# Revit family: S-tank_FRESH-200
name_source: partatom
category: Оборудование
units: mm (PartAtom-declared; Revit-internal decimal feet)

## family parameters
Всегда вертикально = Да
Классификация = Нет
На основе рабочей плоскости = Нет
Общий = Нет
При загрузке вырезать с полостями = Нет
Размер круглого соединителя = Использовать диаметр
Тип детали = Нормальный
Точка расчета площади = Нет

## types (1)
- FRESH 200
    A = 210 мм
    ADSK_URL документации изделия = http://s-tank.ru
    ADSK_Группирование = Оборудование
    ADSK_Единица измерения = шт.
    ADSK_Завод-изготовитель = ООО “С-ТЭНК ВОТЕР ХИТЕРС”
    ADSK_Код изделия = 1.0200
    ADSK_Марка = FRESH 200
    ADSK_Масса = 51
    ADSK_Наименование = Буферная емкость c ГВС
    ADSK_Обозначение = FRESH 200
    B = 355 мм
    C = 465 мм
    D = 545 мм
    DN1 = 25 мм
    DN2 = 15 мм
    E = 625 мм
    H = 935 мм
    I = 735 мм
    a = 130 мм
    shrf = 18 мм
    Диаметрсизоляцией = 780 мм
    Разработка семейств = https://rubim.tech
